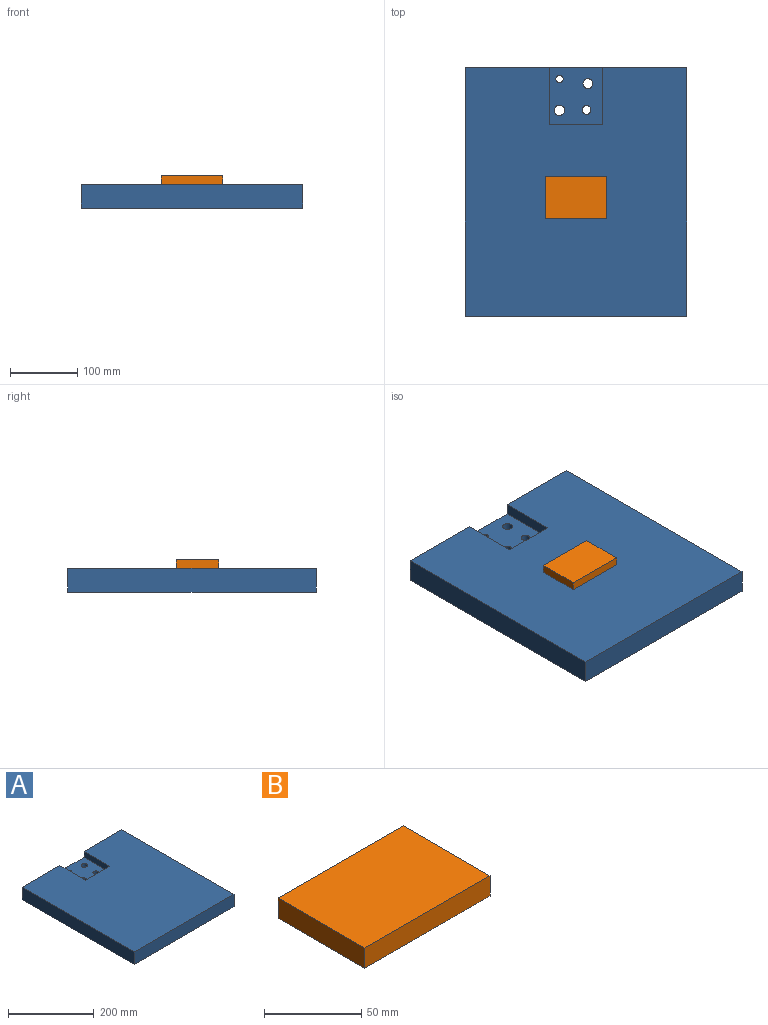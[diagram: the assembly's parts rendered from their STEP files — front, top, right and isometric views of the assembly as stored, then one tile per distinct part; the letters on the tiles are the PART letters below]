
ASSEMBLY  parts=2 mates=1
PART A: 14 faces, bbox 330x370x35.6 mm
  f0: plane 330x35.56mm, normal (0,1,0), area 10374.8mm2, adj f1,f3,f4,f5,f6,f8,f9
  f1: plane 370x35.56mm, normal (-1,0,0), area 13157.2mm2, adj f0,f2,f4,f5
  f2: plane 330x35.56mm, normal (0,-1,0), area 11734.8mm2, adj f1,f3,f4,f5
  f3: plane 370x35.56mm, normal (1,0,0), area 13157.2mm2, adj f0,f2,f4,f5
  f4: plane 370x330mm, normal (0,0,1), area 115300mm2, adj f0,f1,f2,f3,f6,f7,f8
  f5: plane 370x330mm, normal (0,0,-1), area 121518.8mm2, adj f0,f1,f2,f3,f10,f11,f12,f13
  f6: plane 85x17mm, normal (1,0,0), area 1445mm2, adj f0,f4,f7,f9
  f7: plane 80x17mm, normal (0,1,0), area 1360mm2, adj f4,f6,f8,f9
  f8: plane 85x17mm, normal (-1,0,0), area 1445mm2, adj f0,f4,f7,f9
  f9: plane 85x80mm, normal (0,0,1), area 6218.8mm2, adj f0,f6,f7,f8,f10,f11,f12,f13
  f10: cylinder r=5.43mm len=18.56mm, axis (0,0,1), area 633.4mm2, adj f5,f9
  f11: cylinder r=6.5mm len=18.56mm, axis (0,0,1), area 758.1mm2, adj f5,f9
  f12: cylinder r=7.68mm len=18.56mm, axis (0,0,1), area 895.8mm2, adj f5,f9
  f13: cylinder r=7.36mm len=18.56mm, axis (0,0,1), area 858.7mm2, adj f5,f9
PART B: 6 faces, bbox 91x63.1x12.7 mm
  f0: plane 90.96x12.7mm, normal (0,1,0), area 1155.2mm2, adj f1,f3,f4,f5
  f1: plane 63.09x12.7mm, normal (-1,0,0), area 801.3mm2, adj f0,f2,f4,f5
  f2: plane 90.96x12.7mm, normal (0,-1,0), area 1155.2mm2, adj f1,f3,f4,f5
  f3: plane 63.09x12.7mm, normal (1,0,0), area 801.3mm2, adj f0,f2,f4,f5
  f4: plane 90.96x63.09mm, normal (0,0,1), area 5738.8mm2, adj f0,f1,f2,f3
  f5: plane 90.96x63.09mm, normal (0,0,-1), area 5738.8mm2, adj f0,f1,f2,f3
PLACE A at identity
PLACE B t=(0,-193.4,35.56)mm
MATE planar B.f5 <-> A.f4  axis (0,0,-1) through (0,-193.4,35.56)mm
